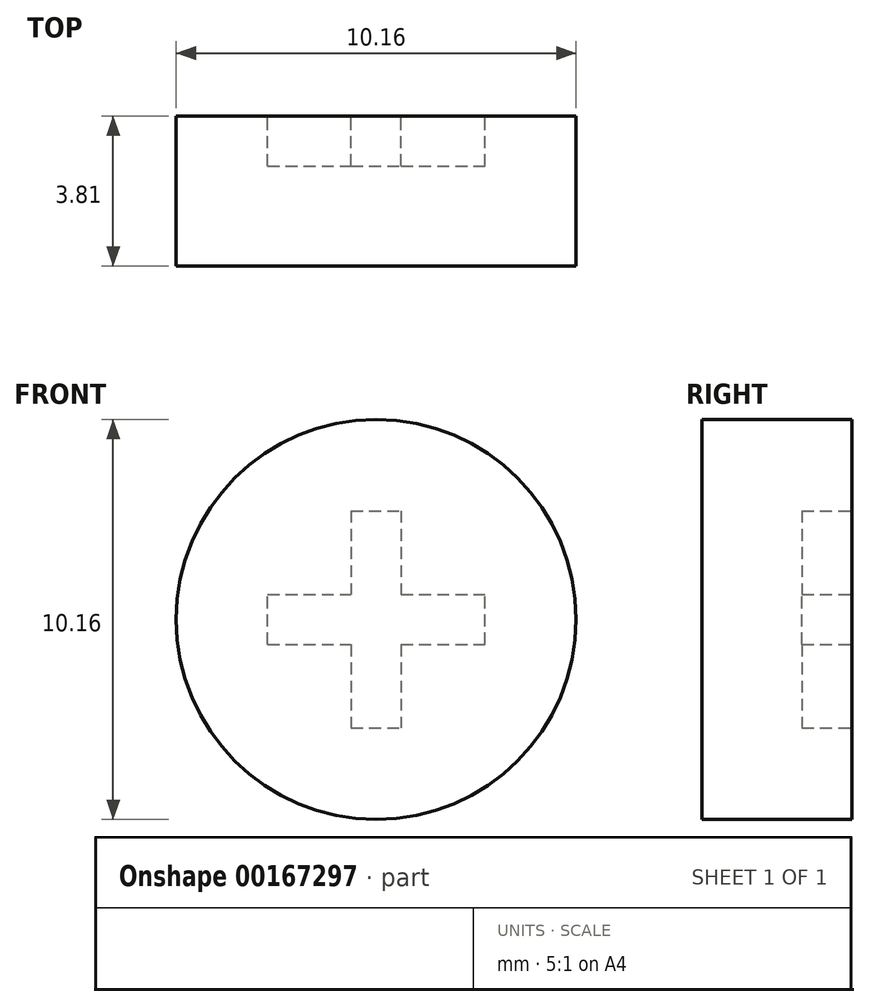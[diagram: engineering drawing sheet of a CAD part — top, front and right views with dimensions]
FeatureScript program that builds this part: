
annotation { "Feature Type Name" : "Feature", "Feature Type Description" : "" }
export const myFeature = defineFeature(function(context is Context, id is Id, definition is map)
    precondition{}
    {
        {
            var Q0;
            Q0=qCreatedBy(makeId("Front.planeOp"),FACE);
            var sketch = newSketch(context, id + "F0", { "sketchPlane" : qUnion([Q0])});
            skCircle(sketch, "E0", {"center": v(0, 0) * mm, "radius": 5.08 * mm});
            skSolve(sketch);
        }
        {
            var Q0;
            Q0=makeQuery(id+"F0.imprint","IMPRINT",FACE,{"disambiguationData":[TD([[makeQuery(id+"F0.imprint","IMPRINT",EDGE,{"derivedFrom":sQuery(id+"F0.wireOp",EDGE,"E0")}),1.0]])]});
            extrude(context, id + "F1", {"entities" : qUnion([Q0]), "depth" : 3.8 * mm});
        }
        {
            var Q0;
            Q0=qCreatedBy(makeId("Front.planeOp"),FACE);
            var sketch = newSketch(context, id + "F2", { "sketchPlane" : qUnion([Q0])});
            skLineSegment(sketch, "E1.bottom", {"start": v(-2.76, -0.64) * mm, "end": v(2.76, -0.64) * mm});
            skLineSegment(sketch, "E1.top", {"start": v(-2.76, 0.64) * mm, "end": v(2.76, 0.64) * mm});
            skLineSegment(sketch, "E1.left", {"start": v(-2.76, -0.64) * mm, "end": v(-2.76, 0.64) * mm});
            skLineSegment(sketch, "E1.right", {"start": v(2.76, -0.64) * mm, "end": v(2.76, 0.64) * mm});
            skPoint(sketch, "E1.middle", {"position": v(0, 0) * mm});
            skLineSegment(sketch, "E2.bottom", {"start": v(-0.64, 2.76) * mm, "end": v(0.63, 2.76) * mm});
            skLineSegment(sketch, "E2.top", {"start": v(-0.63, -2.76) * mm, "end": v(0.64, -2.76) * mm});
            skLineSegment(sketch, "E2.left", {"start": v(-0.64, 2.76) * mm, "end": v(-0.63, -2.76) * mm});
            skLineSegment(sketch, "E2.right", {"start": v(0.63, 2.76) * mm, "end": v(0.64, -2.76) * mm});
            skSolve(sketch);
        }
        {
            var Q0;
            {var subQ0=sQuery(id+"F2.wireOp",EDGE,"E1.left");Q0=makeQuery(id+"F2.imprint","IMPRINT",FACE,{"disambiguationData":[TD([[makeQuery(id+"F2.imprint","IMPRINT",EDGE,{"derivedFrom":subQ0}),-1.0]])]});}
            var Q1;
            {var subQ0=sQuery(id+"F2.wireOp",EDGE,"E2.left");var subQ1=sQuery(id+"F2.wireOp",EDGE,"E1.bottom");var subQ2=makeQuery(id+"F2.imprint","INTERSECT",VERTEX,{"derivedFrom":[subQ1,subQ0]});Q1=makeQuery(id+"F2.imprint","IMPRINT",FACE,{"disambiguationData":[TD([[makeQuery(id+"F2.imprint","IMPRINT",EDGE,{"disambiguationData":[TD([[subQ2,-1.0]])],"derivedFrom":subQ1}),1.0]])]});}
            var Q2;
            {var subQ5=sQuery(id+"F2.wireOp",EDGE,"E2.bottom");Q2=makeQuery(id+"F2.imprint","IMPRINT",FACE,{"disambiguationData":[TD([[makeQuery(id+"F2.imprint","IMPRINT",EDGE,{"derivedFrom":subQ5}),-1.0]])]});}
            var Q3;
            {var subQ0=sQuery(id+"F2.wireOp",EDGE,"E1.right");Q3=makeQuery(id+"F2.imprint","IMPRINT",FACE,{"disambiguationData":[TD([[makeQuery(id+"F2.imprint","IMPRINT",EDGE,{"derivedFrom":subQ0}),1.0]])]});}
            var Q4;
            {var subQ5=sQuery(id+"F2.wireOp",EDGE,"E2.top");Q4=makeQuery(id+"F2.imprint","IMPRINT",FACE,{"disambiguationData":[TD([[makeQuery(id+"F2.imprint","IMPRINT",EDGE,{"derivedFrom":subQ5}),1.0]])]});}
            extrude(context, id + "F3", {"entities" : qUnion([Q0, Q1, Q2, Q3, Q4]), "operationType" : NewBodyOperationType.REMOVE, "depth" : 1.27 * mm});
        }
    });
